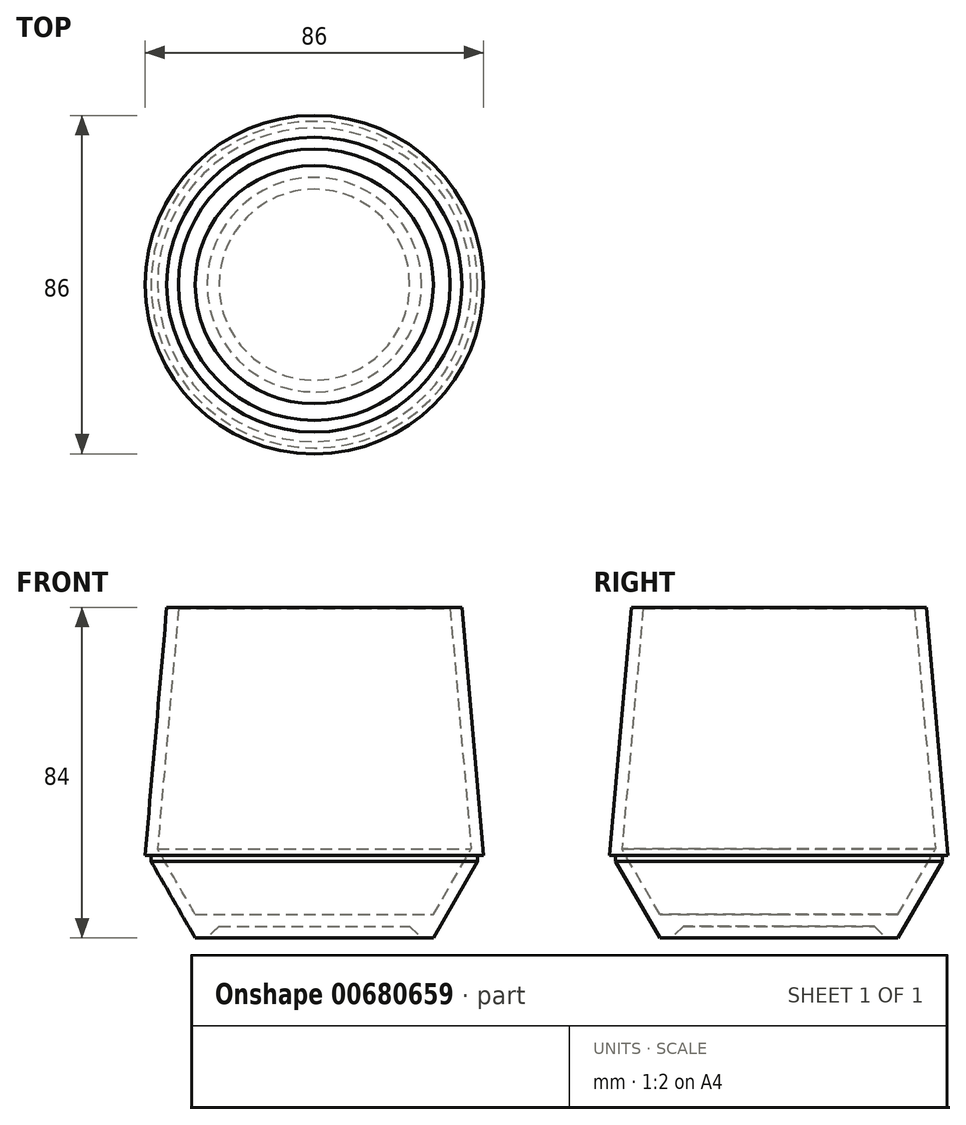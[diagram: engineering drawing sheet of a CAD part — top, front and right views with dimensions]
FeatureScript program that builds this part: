
annotation { "Feature Type Name" : "Feature", "Feature Type Description" : "" }
export const myFeature = defineFeature(function(context is Context, id is Id, definition is map)
    precondition{}
    {
        {
            var Q0;
            Q0=qCreatedBy(makeId("Front.planeOp"),FACE);
            var sketch = newSketch(context, id + "F0", { "sketchPlane" : qUnion([Q0])});
            skLineSegment(sketch, "E0", {"start": v(0, 3) * mm, "end": v(24.24, 3) * mm});
            skLineSegment(sketch, "E1", {"start": v(24.24, 3) * mm, "end": v(27.24, 0) * mm});
            skLineSegment(sketch, "E2", {"start": v(27.24, 0) * mm, "end": v(30.24, 0) * mm});
            skLineSegment(sketch, "E3", {"start": v(30.24, 0) * mm, "end": v(41.5, 19.5) * mm});
            skLineSegment(sketch, "E4", {"start": v(43, 21) * mm, "end": v(37.49, 84) * mm});
            skLineSegment(sketch, "E5", {"start": v(34.5, 83.74) * mm, "end": v(39.85, 22.63) * mm});
            skLineSegment(sketch, "E6", {"start": v(39.85, 22.63) * mm, "end": v(30.24, 6) * mm});
            skLineSegment(sketch, "E7", {"start": v(30.24, 6) * mm, "end": v(0, 6) * mm});
            skLineSegment(sketch, "E8", {"start": v(0, 6) * mm, "end": v(0, 3) * mm});
            skPoint(sketch, "E9.visualSharp", {"position": v(24.24, 3) * mm});
            skPoint(sketch, "E10.visualSharp", {"position": v(39.85, 22.63) * mm});
            skLineSegment(sketch, "E11", {"start": v(0, 0) * mm, "end": v(0, 84) * mm, "construction": true});
            skLineSegment(sketch, "E12", {"start": v(41.5, 19.5) * mm, "end": v(41.5, 21) * mm});
            skLineSegment(sketch, "E13", {"start": v(43, 0) * mm, "end": v(43, 84) * mm, "construction": true});
            skLineSegment(sketch, "E14", {"start": v(34.5, 83.74) * mm, "end": v(37.49, 84) * mm});
            skLineSegment(sketch, "E15", {"start": v(41.5, 21) * mm, "end": v(43, 21) * mm});
            skSolve(sketch);
        }
        {
            var Q0;
            Q0=qSketchRegion(id+"F0",true);
            var Q1;
            Q1=sQuery(id+"F0.wireOp",EDGE,"E11");
            revolve(context, id + "F1", {"entities" : qUnion([Q0]), "axis" : qUnion([Q1]), "revolveType" : RevolveType.FULL});
        }
    });
